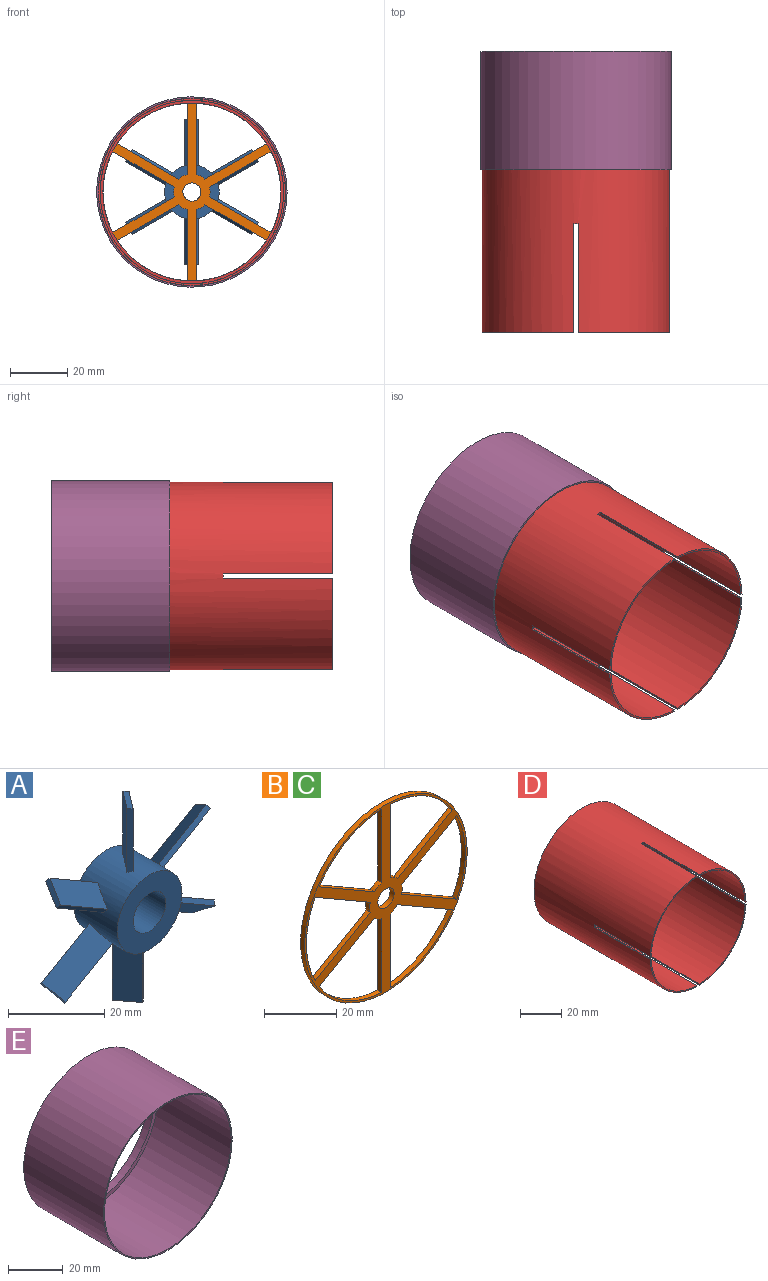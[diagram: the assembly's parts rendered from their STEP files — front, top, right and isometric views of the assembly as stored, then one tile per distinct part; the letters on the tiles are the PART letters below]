
ASSEMBLY  parts=5 mates=8
PART A: 34 faces, bbox 46.4x12.7x50.8 mm
  f0: cylinder r=9.53mm len=19.05mm, axis (0,1,0), area 711.3mm2, adj f1,f2,f3,f4,f5,f6,f8,f9
  f1: plane 19.05x19.05mm, normal (0,-1,0), area 213.8mm2, adj f0,f33
  f2: plane 19.05x19.05mm, normal (0,1,0), area 213.8mm2, adj f0,f33
  f3: plane 15.78x11.45mm, normal (-0.4,0.61,-0.69), area 101.3mm2, adj f0,f4,f6,f7
  f4: plane 14.35x8.97mm, normal (-0.3,-0.79,-0.53), area 20.4mm2, adj f0,f3,f5,f7
  f5: plane 15.96x11.34mm, normal (0.4,-0.61,0.69), area 101.3mm2, adj f0,f4,f6,f7
  f6: plane 14.53x8.87mm, normal (0.3,0.79,0.53), area 20.4mm2, adj f0,f3,f5,f7
  f7: plane 5.81x4.22mm, normal (-0.87,0,0.5), area 8.1mm2, adj f3,f4,f5,f6
  f8: plane 15.96x11.34mm, normal (0.4,0.61,-0.69), area 101.3mm2, adj f0,f9,f11,f12
  f9: plane 14.53x8.87mm, normal (0.3,-0.79,-0.53), area 20.4mm2, adj f0,f8,f10,f12
  f10: plane 15.78x11.45mm, normal (-0.4,-0.61,0.69), area 101.3mm2, adj f0,f9,f11,f12
  f11: plane 14.35x8.97mm, normal (-0.3,0.79,0.53), area 20.4mm2, adj f0,f8,f10,f12
  f12: plane 5.81x4.22mm, normal (-0.87,0,-0.5), area 8.1mm2, adj f8,f9,f10,f11
  f13: plane 16.19x5.04mm, normal (0.79,0.61,0), area 101.3mm2, adj f0,f14,f16,f17
  f14: plane 16.2x1.01mm, normal (0.61,-0.79,0), area 20.4mm2, adj f0,f13,f15,f17
  f15: plane 16.19x5.04mm, normal (-0.79,-0.61,0), area 101.3mm2, adj f0,f14,f16,f17
  f16: plane 16.2x1.01mm, normal (-0.61,0.79,0), area 20.4mm2, adj f0,f13,f15,f17
  f17: plane 5.81x4.88mm, normal (0,0,-1), area 8.1mm2, adj f13,f14,f15,f16
  f18: plane 15.78x11.45mm, normal (0.4,0.61,0.69), area 101.3mm2, adj f0,f19,f21,f22
  f19: plane 14.35x8.97mm, normal (0.3,-0.79,0.53), area 20.4mm2, adj f0,f18,f20,f22
  f20: plane 15.96x11.34mm, normal (-0.4,-0.61,-0.69), area 101.3mm2, adj f0,f19,f21,f22
  f21: plane 14.53x8.87mm, normal (-0.3,0.79,-0.53), area 20.4mm2, adj f0,f18,f20,f22
  f22: plane 5.81x4.22mm, normal (0.87,0,-0.5), area 8.1mm2, adj f18,f19,f20,f21
  f23: plane 15.96x11.34mm, normal (-0.4,0.61,0.69), area 101.3mm2, adj f0,f24,f26,f27
  f24: plane 14.53x8.87mm, normal (-0.3,-0.79,0.53), area 20.4mm2, adj f0,f23,f25,f27
  f25: plane 15.78x11.45mm, normal (0.4,-0.61,-0.69), area 101.3mm2, adj f0,f24,f26,f27
  f26: plane 14.35x8.97mm, normal (0.3,0.79,-0.53), area 20.4mm2, adj f0,f23,f25,f27
  f27: plane 5.81x4.22mm, normal (0.87,0,0.5), area 8.1mm2, adj f23,f24,f25,f26
  f28: plane 16.19x5.04mm, normal (-0.79,0.61,0), area 101.3mm2, adj f0,f29,f31,f32
  f29: plane 16.2x1.01mm, normal (-0.61,-0.79,0), area 20.4mm2, adj f0,f28,f30,f32
  f30: plane 16.19x5.04mm, normal (0.79,-0.61,0), area 101.3mm2, adj f0,f29,f31,f32
  f31: plane 16.2x1.01mm, normal (0.61,0.79,0), area 20.4mm2, adj f0,f28,f30,f32
  f32: plane 5.81x4.88mm, normal (0,0,1), area 8.1mm2, adj f28,f29,f30,f31
  f33: cylinder r=4.76mm len=12.7mm, axis (0,-1,0), area 380mm2, adj f1,f2
PART B: 28 faces, bbox 63.5x1.6x63.5 mm
  f0: cylinder r=31.05mm len=28.26mm, axis (0,1,0), area 46.6mm2, adj f1,f18,f25,f26
  f1: plane 21.53x12.43mm, normal (-0.5,0,-0.87), area 39.5mm2, adj f0,f2,f25,f26
  f2: cylinder r=6.35mm len=3.4mm, axis (0,1,0), area 5.5mm2, adj f1,f18,f25,f26
  f3: cylinder r=31.05mm len=24.48mm, axis (0,1,0), area 46.6mm2, adj f4,f19,f25,f26
  f4: plane 24.86x1.59mm, normal (1,0,0), area 39.5mm2, adj f3,f5,f25,f26
  f5: cylinder r=6.35mm len=2.94mm, axis (0,1,0), area 5.5mm2, adj f4,f19,f25,f26
  f6: cylinder r=31.05mm len=28.26mm, axis (0,1,0), area 46.6mm2, adj f7,f20,f25,f26
  f7: plane 21.53x12.43mm, normal (0.5,0,0.87), area 39.5mm2, adj f6,f8,f25,f26
  f8: cylinder r=6.35mm len=3.4mm, axis (0,1,0), area 5.5mm2, adj f7,f20,f25,f26
  f9: cylinder r=31.05mm len=24.48mm, axis (0,1,0), area 46.6mm2, adj f10,f21,f25,f26
  f10: plane 21.53x12.43mm, normal (-0.5,0,0.87), area 39.5mm2, adj f9,f11,f25,f26
  f11: cylinder r=6.35mm len=2.94mm, axis (0,1,0), area 5.5mm2, adj f10,f21,f25,f26
  f12: cylinder r=31.05mm len=24.48mm, axis (0,1,0), area 46.6mm2, adj f13,f22,f25,f26
  f13: plane 21.53x12.43mm, normal (0.5,0,-0.87), area 39.5mm2, adj f12,f14,f25,f26
  f14: cylinder r=6.35mm len=2.94mm, axis (0,1,0), area 5.5mm2, adj f13,f22,f25,f26
  f15: cylinder r=6.35mm len=2.94mm, axis (0,1,0), area 5.5mm2, adj f16,f23,f25,f26
  f16: plane 21.53x12.43mm, normal (0.5,0,0.87), area 39.5mm2, adj f15,f17,f25,f26
  f17: cylinder r=31.05mm len=24.48mm, axis (0,1,0), area 46.6mm2, adj f16,f23,f25,f26
  f18: plane 21.53x12.43mm, normal (-0.5,0,0.87), area 39.5mm2, adj f0,f2,f25,f26
  f19: plane 21.53x12.43mm, normal (-0.5,0,-0.87), area 39.5mm2, adj f3,f5,f25,f26
  f20: plane 21.53x12.43mm, normal (0.5,0,-0.87), area 39.5mm2, adj f6,f8,f25,f26
  f21: plane 24.86x1.59mm, normal (1,0,0), area 39.5mm2, adj f9,f11,f25,f26
  f22: plane 24.86x1.59mm, normal (-1,0,0), area 39.5mm2, adj f12,f14,f25,f26
  f23: plane 24.86x1.59mm, normal (-1,0,0), area 39.5mm2, adj f15,f17,f25,f26
  f24: cylinder r=31.75mm len=63.5mm, axis (0,1,0), area 316.7mm2, adj f25,f26
  f25: plane 63.5x63.5mm, normal (0,-1,0), area 704.4mm2, adj f0,f1,f2,f3,f4,f5,f6,f7
  f26: plane 63.5x63.5mm, normal (0,1,0), area 704.4mm2, adj f0,f1,f2,f3,f4,f5,f6,f7
  f27: cylinder r=3.17mm len=6.35mm, axis (0,-1,0), area 31.7mm2, adj f25,f26
PART C: same geometry as B
PART D: 21 faces, bbox 65.4x79.4x65.4 mm
  f0: plane 31.9x31.9mm, normal (0,-1,0), area 31.3mm2, adj f3,f4,f8,f11
  f1: plane 31.9x31.9mm, normal (0,-1,0), area 31.3mm2, adj f3,f4,f10,f14
  f2: plane 31.9x31.9mm, normal (0,-1,0), area 31.3mm2, adj f3,f4,f13,f16
  f3: cylinder r=32.07mm len=76.2mm, axis (0,-1,0), area 15111.3mm2, adj f0,f1,f2,f5,f6,f7,f8,f9
  f4: cylinder r=32.7mm len=79.38mm, axis (0,-1,0), area 16067.7mm2, adj f0,f1,f2,f5,f6,f7,f8,f9
  f5: plane 31.9x31.9mm, normal (0,-1,0), area 31.3mm2, adj f3,f4,f7,f17
  f6: plane 1.59x0.65mm, normal (0,-1,0), area 1mm2, adj f3,f4,f7,f8
  f7: plane 38.1x0.64mm, normal (1,0,0), area 24.2mm2, adj f3,f4,f5,f6
  f8: plane 38.1x0.64mm, normal (-1,0,0), area 24.2mm2, adj f0,f3,f4,f6
  f9: plane 1.59x0.65mm, normal (0,-1,0), area 1mm2, adj f3,f4,f10,f11
  f10: plane 38.1x0.64mm, normal (0,0,-1), area 24.2mm2, adj f1,f3,f4,f9
  f11: plane 38.1x0.64mm, normal (0,0,1), area 24.2mm2, adj f0,f3,f4,f9
  f12: plane 1.59x0.65mm, normal (0,-1,0), area 1mm2, adj f3,f4,f13,f14
  f13: plane 38.1x0.64mm, normal (1,0,0), area 24.2mm2, adj f2,f3,f4,f12
  f14: plane 38.1x0.64mm, normal (-1,0,0), area 24.2mm2, adj f1,f3,f4,f12
  f15: plane 1.59x0.65mm, normal (0,-1,0), area 1mm2, adj f3,f4,f16,f17
  f16: plane 38.1x0.64mm, normal (0,0,-1), area 24.2mm2, adj f2,f3,f4,f15
  f17: plane 38.1x0.64mm, normal (0,0,1), area 24.2mm2, adj f3,f4,f5,f15
  f18: plane 64.14x64.14mm, normal (0,-1,0), area 189.1mm2, adj f3,f19
  f19: cylinder r=31.12mm len=62.23mm, axis (0,-1,0), area 620.7mm2, adj f18,f20
  f20: plane 65.41x65.41mm, normal (0,1,0), area 318.3mm2, adj f4,f19
PART E: 6 faces, bbox 66.5x41.3x66.5 mm
  f0: cylinder r=32.77mm len=65.53mm, axis (0,-1,0), area 7843.8mm2, adj f2,f3
  f1: cylinder r=33.27mm len=66.55mm, axis (0,-1,0), area 8629.2mm2, adj f2,f5
  f2: plane 66.55x66.55mm, normal (0,-1,0), area 105.4mm2, adj f0,f1
  f3: plane 65.53x65.53mm, normal (0,-1,0), area 331.3mm2, adj f0,f4
  f4: cylinder r=31.12mm len=62.23mm, axis (0,-1,0), area 620.7mm2, adj f3,f5
  f5: plane 66.55x66.55mm, normal (0,1,0), area 436.7mm2, adj f1,f4
PLACE A t=(-110.05,44.29,-131.78)mm
PLACE B t=(-110.05,37.94,-131.78)mm
PLACE C t=(-110.05,52.22,-131.78)mm
PLACE D t=(-110.05,-42.79,-131.78)mm
PLACE E t=(-110.05,14.12,-131.78)mm
MATE fastened C.f0 <-> E.f0  axis (0,1,0) through (-110.05,52.22,-131.78)mm
MATE fastened B.f0 <-> A.f0  axis (0,-1,0) through (-110.05,37.94,-131.78)mm
MATE cylindrical B.f0 <-> C.f0  axis (0,1,0) through (-110.05,37.14,-131.78)mm
MATE cylindrical A.f0 <-> C.f0  axis (0,1,0) through (-110.05,50.64,-131.78)mm
MATE cylindrical A.f0 <-> B.f0  axis (0,-1,0) through (-110.05,37.94,-131.78)mm
MATE slider E.f0 <-> D.f3  axis (0,-1,0) through (-110.05,33.17,-131.78)mm
MATE cylindrical E.f0 <-> D.f3  axis (0,-1,0) through (-110.05,34.76,-131.78)mm
MATE fastened C.f0 <-> A.f0  axis (0,-1,0) through (-110.05,50.64,-131.78)mm
